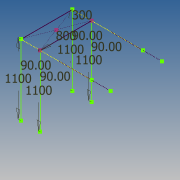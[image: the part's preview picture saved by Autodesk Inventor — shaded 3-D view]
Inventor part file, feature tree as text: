
AUTODESK INVENTOR PART (.ipt)
format: ipt  version: 2019 (Build 230136000, 136)  size: 84,480 bytes
history: native  units: mm
features: sketch x4
ambient origin geometry x8: Origin, YZ Plane, XZ Plane, XY Plane, X Axis, Y Axis, Z Axis, Center Point
feature tree (4):
  sketch  "Sketch1"  dims[d0=300.0mm d1=800.0mm d2=1100.0mm d3=90.0deg d4=1100.0mm d5=90.0deg d6=1100.0mm d7=90.0deg d8=1100.0mm d9=90.0deg]
  sketch  "3D Sketch1"
  sketch  "3D Sketch2"
  sketch  "3D Sketch3"
